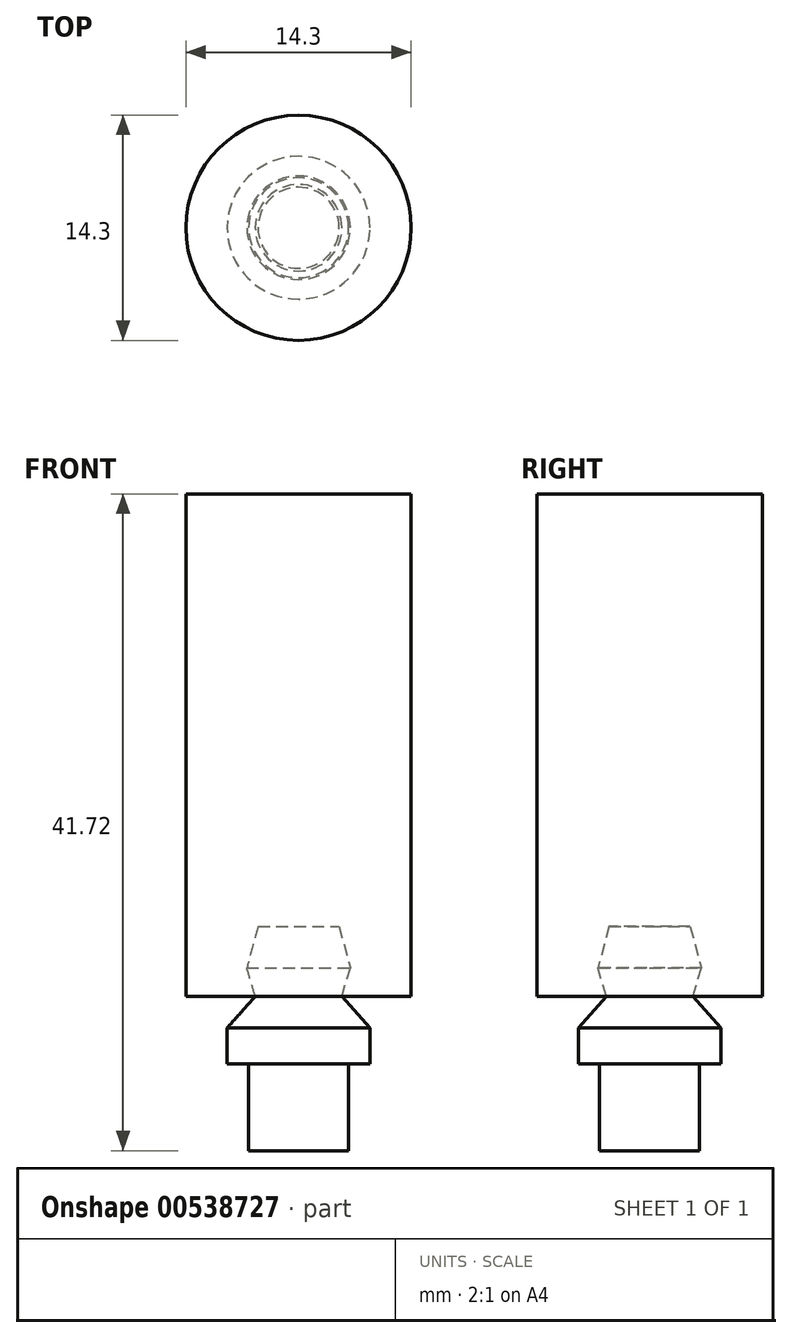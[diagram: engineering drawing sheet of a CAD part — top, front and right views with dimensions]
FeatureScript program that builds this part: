
annotation { "Feature Type Name" : "Feature", "Feature Type Description" : "" }
export const myFeature = defineFeature(function(context is Context, id is Id, definition is map)
    precondition{}
    {
        {
            var Q0;
            Q0=qCreatedBy(makeId("Front.planeOp"),FACE);
            var sketch = newSketch(context, id + "F0", { "sketchPlane" : qUnion([Q0])});
            skLineSegment(sketch, "E0", {"start": v(0, 8.73) * mm, "end": v(2.58, 8.73) * mm});
            skLineSegment(sketch, "E1", {"start": v(2.58, 8.73) * mm, "end": v(3.29, 6.1) * mm});
            skLineSegment(sketch, "E2", {"start": v(3.28, 6.1) * mm, "end": v(2.75, 4.3) * mm});
            skLineSegment(sketch, "E3", {"start": v(2.75, 4.3) * mm, "end": v(4.54, 2.3) * mm});
            skLineSegment(sketch, "E4", {"start": v(4.54, 2.3) * mm, "end": v(4.54, 0) * mm});
            skLineSegment(sketch, "E5", {"start": v(4.54, 0) * mm, "end": v(3.18, 0) * mm});
            skLineSegment(sketch, "E6", {"start": v(3.18, 0) * mm, "end": v(3.18, -5.5) * mm});
            skLineSegment(sketch, "E7", {"start": v(3.18, -5.5) * mm, "end": v(0, -5.5) * mm});
            skLineSegment(sketch, "E8", {"start": v(0, -5.5) * mm, "end": v(0, 8.73) * mm});
            skSolve(sketch);
        }
        {
            var Q0;
            Q0 = qSketchRegion(id + "F0", true);
            var Q1;
            Q1=sQuery(id+"F0.wireOp",EDGE,"E8");
            revolve(context, id + "F1", {"entities" : qUnion([Q0]), "axis" : qUnion([Q1]), "revolveType" : RevolveType.FULL});
        }
        {
            var Q0;
            Q0=qCreatedBy(makeId("Front.planeOp"),FACE);
            var sketch = newSketch(context, id + "F2", { "sketchPlane" : qUnion([Q0])});
            skLineSegment(sketch, "E9.bottom", {"start": v(7.15, 36.22) * mm, "end": v(0, 36.22) * mm});
            skLineSegment(sketch, "E9.top", {"start": v(7.15, 4.3) * mm, "end": v(0, 4.3) * mm});
            skLineSegment(sketch, "E9.left", {"start": v(7.15, 36.22) * mm, "end": v(7.15, 4.3) * mm});
            skLineSegment(sketch, "E10", {"start": v(0, 36.22) * mm, "end": v(0, 4.3) * mm});
            skPoint(sketch, "E11.orphan", {"position": v(-7.15, 36.22) * mm});
            skPoint(sketch, "E12.orphan", {"position": v(-7.15, 4.3) * mm});
            skSolve(sketch);
        }
        {
            var Q0;
            Q0=makeQuery(id+"F2.imprint","IMPRINT",FACE,{"disambiguationData":[TD([[makeQuery(id+"F2.imprint","IMPRINT",EDGE,{"derivedFrom":sQuery(id+"F2.wireOp",EDGE,"E9.bottom")}),1.0]])]});
            var Q1;
            Q1=sQuery(id+"F2.wireOp",EDGE,"E10");
            revolve(context, id + "F3", {"entities" : qUnion([Q0]), "axis" : qUnion([Q1]), "revolveType" : RevolveType.FULL});
        }
    });
